# Revit family: External block R080_R160_1R1A
name_source: partatom
category: Оборудование
units: mm (PartAtom-declared; Revit-internal decimal feet)

## family parameters
Всегда вертикально = Да
Классификация = Нет
На основе рабочей плоскости = Нет
Общий = Нет
При загрузке вырезать с полостями = Нет
Размер круглого соединителя = Использовать диаметр
Тип детали = Нормальный
Точка принадлежности помещению = Нет

## types (5) — shared parameters
00_20_Manufacturer = BLAUBERG
00_20_Name = External block
Casing Material = Steel, white, mat
Electric = Нет
Grid Material = Mesh, steel, painted,  white
Load Classification = HVAC
Maintenance zone material = <По категории>
Maximum Air Flow = 0.0 л/с
d = 10 мм
d1 = 16 мм
rn = 10 мм
Изготовитель = BLAUBERG
zero-valued in all types: Отметка по умолчанию

## per-type parameters (varying)
| type | Dv | H | Height | L | Lb | Length | Ln | Lv | Power | Wb | Weight | Width | Wn | h | wn |
| BLHV-R100-O/1R1A | 660 мм | 810 мм | 810 мм | 1032 мм | 982 мм | 1032 мм | 445 мм | 111 мм | 3100 Вт | 400 мм | 60.00 кг | 445 мм | 670 мм | 790 мм | 310 мм |
| BLHV-R080-O/1R1A | 552 мм | 702 мм | 702 мм | 935 мм | 885 мм | 935 мм | 383 мм | 117 мм | 2650 Вт | 353 мм | 47.00 кг | 383 мм | 544 мм | 682 мм | 247 мм |
| BLHV-R125-O/1R1A | 660 мм | 810 мм | 810 мм | 1032 мм | 982 мм | 1032 мм | 445 мм | 111 мм | 3520 Вт | 400 мм | 85.00 кг | 445 мм | 670 мм | 790 мм | 310 мм |
| BLHV-R140-O/1R1A | 720 мм | 870 мм | 870 мм | 1100 мм | 1050 мм | 1100 мм | 528 мм | 115 мм | 4000 Вт | 485 мм | 90.00 кг | 528 мм | 635 мм | 850 мм | 293 мм |
| BLHV-R160-O/1R1A | 720 мм | 870 мм | 870 мм | 1100 мм | 1050 мм | 1100 мм | 528 мм | 115 мм | 4400 Вт | 485 мм | 90.00 кг | 528 мм | 635 мм | 850 мм | 293 мм |

note: column(s) folded — value = type name in every type: 00_20_Type
